# Revit family: Wall_Plate-GROHE-Skate_Cosmopolitan-38732_Series
name_source: partatom
category: Specialty Equipment
revit_build: Autodesk Revit 2014 (Build: 20130308_1515(x64)
units: mm (PartAtom-declared; Revit-internal decimal feet)

## types (5) — shared parameters
Assembly Code = C1030200
CW Connection = Yes
CWFU = 1.5
Default Elevation = 40"
Description = Skate Cosmopolitan Wall Plate
HW Connection = Yes
HWFU = 1.5
Height = 7 3/4"
Installation Type = Wall Mounted
Length = 23/32"
Manufacturer = Grohe
Price = Prices may vary. Please consult Manufacturer Representative for most up-to-date price list.
Product Page URL = https://www.grohe.us
URL = https://www.grohe.us
Vent Connection = No
WFU = 2
Warranty Documentation Link = https://cdn.cloud.grohe.com
Waste Connection = No
Width = 6 5/32"

## per-type parameters (varying)
| type | Finish | Material |
| 38732000 | Metal-Grohe-000-Chrome | Metal-Grohe-000-Chrome |
| 38732P00 | Metal-Grohe-P00-Matte Chrome | Metal-Grohe-P00-Matte Chrome |
| 38732SH0 | Metal-Grohe-SH0-Alpine White | Metal-Grohe-SH0-Alpine White |
| 38732EN0 | Metal-Grohe-EN0-Brushed Nickel | Metal-Grohe-EN0-Brushed Nickel |
| 38732BE0 | Metal-Grohe-BE0-Nickel | Metal-Grohe-BE0-Nickel |

note: column(s) folded — value = type name in every type: Model

## geometry (parser evidence)
native form markers: Sweep x3
no freeform markers — native parametric forms only
